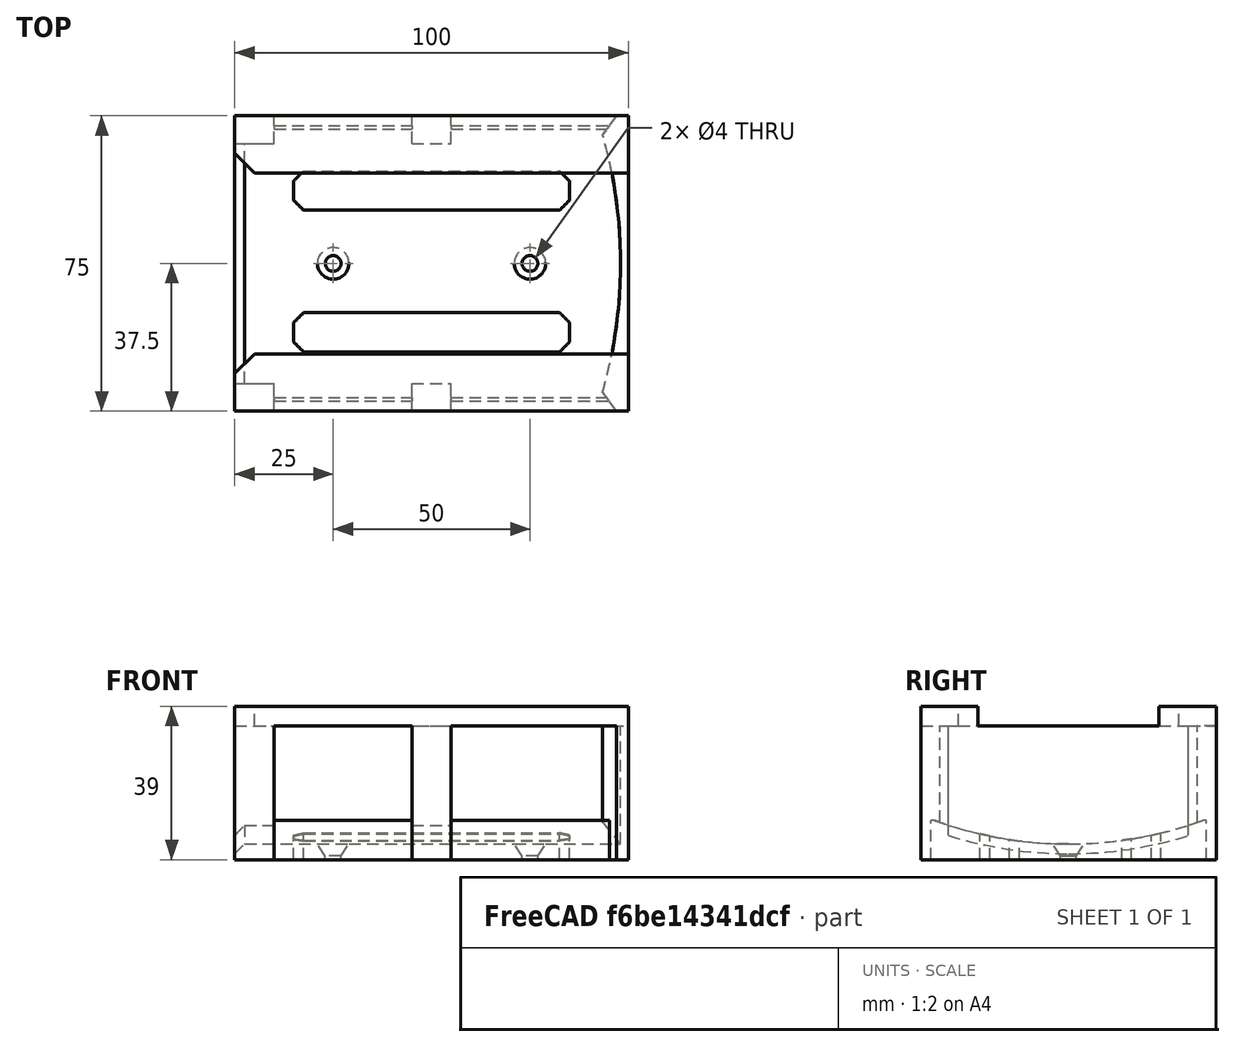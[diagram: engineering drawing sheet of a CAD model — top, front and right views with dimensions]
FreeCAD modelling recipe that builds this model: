
FCSTD DOCUMENT  (FreeCAD 0.19R24276 (Git))
Label: lennox-remote-holder
License: All rights reserved
LicenseURL: http://en.wikipedia.org/wiki/All_rights_reserved
objects: Part::Box×10, Part::Cylinder×6, Part::MultiFuse×6, Part::Chamfer×5, Part::Cut×4, Part::Cone×2
note: 33 computed .brp shape members not serialized (recipe doc carries the construction recipe); baked Part::Feature solids carry a one-line shape summary decoded from their .brp

FEATURE [Part::Box] Box  label="Cube"
  AttacherType = Attacher::AttachEngine3D
  Height = 10
  Length = 100
  Width = 70
FEATURE [Part::Cylinder] Cylinder
  Angle = 360
  AttacherType = Attacher::AttachEngine3D
  Height = 100
  Placement = pos=(0,35,104) rot=(0,1,0;1.5708rad)
  Radius = 100
FEATURE [Part::Cut] Cut
  Base = -> Box
  Tool = -> Cylinder
FEATURE [Part::Box] Box001  label="Cube001"
  AttacherType = Attacher::AttachEngine3D
  Height = 34
  Length = 10
  Placement = pos=(90,-2.5,0) rot=(0,0,1;0rad)
  Width = 75
FEATURE [Part::Cylinder] Cylinder001
  Angle = 360
  AttacherType = Attacher::AttachEngine3D
  Height = 40
  Placement = pos=(-22,35,0) rot=(0,0,1;0rad)
  Radius = 120
FEATURE [Part::Cut] Cut001
  Base = -> Box001
  Tool = -> Cylinder001
FEATURE [Part::Box] Box002  label="Cube002"
  AttacherType = Attacher::AttachEngine3D
  Height = 34
  Length = 10
  Placement = pos=(0,65.5,0) rot=(0,0,1;0rad)
  Width = 7
FEATURE [Part::Box] Box003  label="Cube003"
  AttacherType = Attacher::AttachEngine3D
  Height = 5
  Length = 100
  Placement = pos=(0,58,34) rot=(0,0,1;0rad)
  Width = 14.5
FEATURE [Part::Box] Box004  label="Cube004"
  AttacherType = Attacher::AttachEngine3D
  Height = 34
  Length = 10
  Placement = pos=(45,65.5,0) rot=(0,0,1;0rad)
  Width = 7
FEATURE [Part::Box] Box005  label="Cube005"
  AttacherType = Attacher::AttachEngine3D
  Height = 34
  Length = 10
  Placement = pos=(0,-2.5,0) rot=(0,0,1;0rad)
  Width = 7
FEATURE [Part::Box] Box006  label="Cube006"
  AttacherType = Attacher::AttachEngine3D
  Height = 34
  Length = 10
  Placement = pos=(45,-2.5,0) rot=(0,0,1;0rad)
  Width = 7
FEATURE [Part::Box] Box007  label="Cube007"
  AttacherType = Attacher::AttachEngine3D
  Height = 5
  Length = 100
  Placement = pos=(0,-2.5,34) rot=(0,0,1;0rad)
  Width = 14.5
FEATURE [Part::Cylinder] Cylinder002
  Angle = 360
  AttacherType = Attacher::AttachEngine3D
  Height = 10
  Placement = pos=(0,35,13) rot=(0,0,1;0rad)
  Radius = 4
FEATURE [Part::Cone] Cone
  Angle = 360
  AttacherType = Attacher::AttachEngine3D
  Height = 3
  Placement = pos=(0,35,10) rot=(0,0,1;0rad)
  Radius1 = 2
  Radius2 = 4
FEATURE [Part::Cylinder] Cylinder003
  Angle = 360
  AttacherType = Attacher::AttachEngine3D
  Height = 10
  Placement = pos=(0,35,0) rot=(0,0,1;0rad)
  Radius = 2
FEATURE [Part::MultiFuse] Fusion  label="countersink mount"
  Placement = pos=(25,0,-9) rot=(0,0,1;0rad)
  Shapes = -> [Cylinder002,Cone,Cylinder003]
FEATURE [Part::Cylinder] Cylinder004
  Angle = 360
  AttacherType = Attacher::AttachEngine3D
  Height = 10
  Placement = pos=(0,35,13) rot=(0,0,1;0rad)
  Radius = 4
FEATURE [Part::Cylinder] Cylinder005
  Angle = 360
  AttacherType = Attacher::AttachEngine3D
  Height = 10
  Placement = pos=(0,35,0) rot=(0,0,1;0rad)
  Radius = 2
FEATURE [Part::Cone] Cone001
  Angle = 360
  AttacherType = Attacher::AttachEngine3D
  Height = 3
  Placement = pos=(0,35,10) rot=(0,0,1;0rad)
  Radius1 = 2
  Radius2 = 4
FEATURE [Part::MultiFuse] Fusion001  label="countersink mount001"
  Placement = pos=(75,0,-9) rot=(0,0,1;0rad)
  Shapes = -> [Cylinder004,Cone001,Cylinder005]
FEATURE [Part::MultiFuse] Fusion002
  Shapes = -> [Fusion,Fusion001]
FEATURE [Part::Cut] Cut002
  Base = -> Cut
  Tool = -> Fusion002
FEATURE [Part::Box] Box008  label="Cube008"
  AttacherType = Attacher::AttachEngine3D
  Height = 10
  Length = 70
  Width = 10
FEATURE [Part::MultiFuse] Fusion003
  Shapes = -> [Box007,Box002,Box003,Box004,Box005,Box006]
FEATURE [Part::Chamfer] Chamfer
  Base = -> Box008
  Edges = 4 edges r=2.5: [Edge1,Edge3,Edge5,Edge7]
  Placement = pos=(15,12.5,0) rot=(0,0,1;0rad)
FEATURE [Part::Box] Box009  label="Cube009"
  AttacherType = Attacher::AttachEngine3D
  Height = 10
  Length = 70
  Width = 10
FEATURE [Part::Chamfer] Chamfer001
  Base = -> Box009
  Edges = 4 edges r=2.5: [Edge1,Edge3,Edge5,Edge7]
  Placement = pos=(15,48.5,0) rot=(0,0,1;0rad)
FEATURE [Part::MultiFuse] Fusion004
  Shapes = -> [Chamfer001,Chamfer]
FEATURE [Part::Cut] Cut003
  Base = -> Cut002
  Tool = -> Fusion004
FEATURE [Part::Chamfer] Chamfer004
  Base = -> Cut001
  Edges = 2 edges r=5: [Edge4,Edge15]
FEATURE [Part::Chamfer] Chamfer012
  Base = -> Cut003
  Edges = 2 edges r=2.5: [Edge2,Edge3]
FEATURE [Part::MultiFuse] Fusion005
  Shapes = -> [Fusion003,Chamfer004,Chamfer012]
FEATURE [Part::Chamfer] Chamfer013
  Base = -> Fusion005
  Edges = 2 edges r=5: [Edge3,Edge89]
